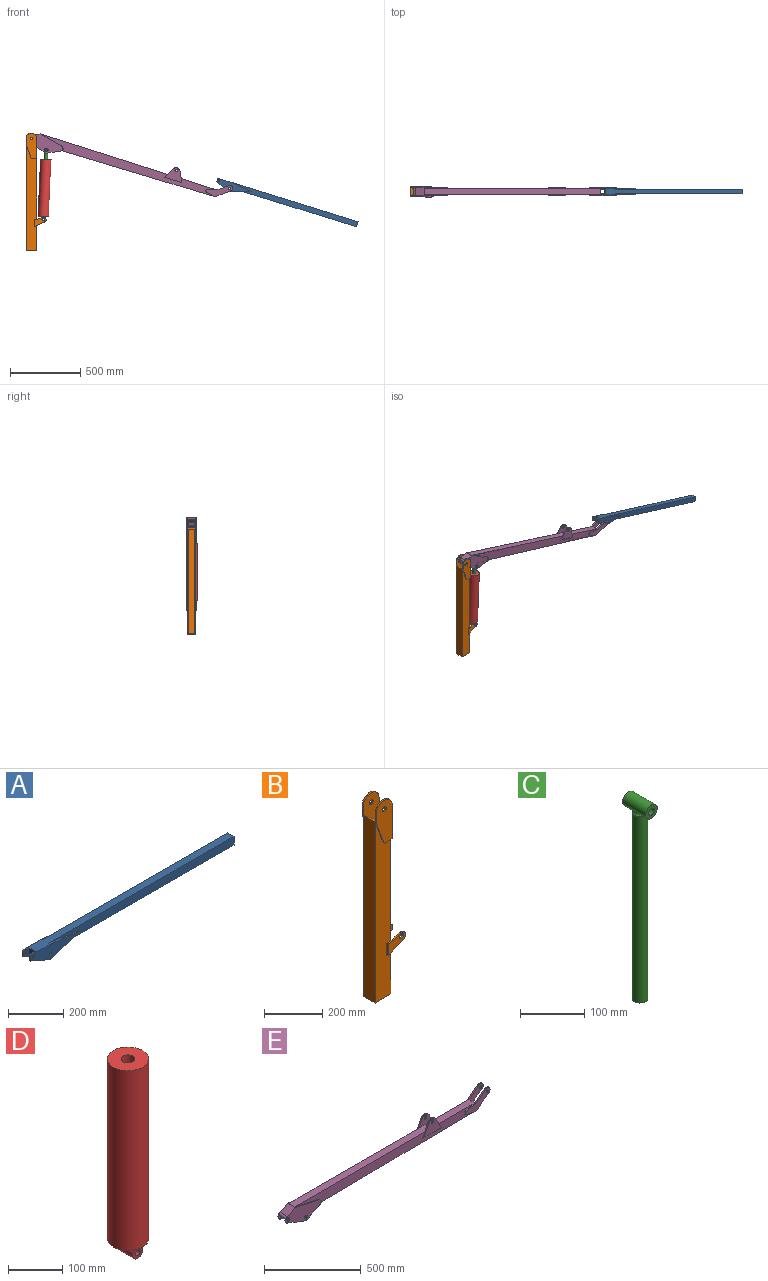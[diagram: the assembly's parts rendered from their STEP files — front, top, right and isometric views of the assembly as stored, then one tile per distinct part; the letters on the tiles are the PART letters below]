
ASSEMBLY  parts=5 mates=5
PART A: 24 faces, bbox 1045.2x44.5x69.9 mm
  f0: plane 945.69x38.1mm, normal (0,-1,0), area 32165.4mm2, adj f1,f3,f4,f7,f8
  f1: plane 1045.2x44.45mm, normal (0,0,1), area 33521.7mm2, adj f0,f2,f4,f5,f8,f10,f13,f14
  f2: plane 38.1x31.75mm, normal (-1,0,0), area 1209.7mm2, adj f1,f3,f5,f15
  f3: plane 1016x31.75mm, normal (0,0,-1), area 32258mm2, adj f0,f2,f4,f12,f14,f22
  f4: plane 38.1x31.75mm, normal (1,0,0), area 1209.7mm2, adj f0,f1,f3,f14
  f5: plane 38.1x29.2mm, normal (0,1,0), area 800.3mm2, adj f1,f2,f6,f9,f10
  f6: plane 102.19x44.45mm, normal (-0.4,0,-0.92), area 707.6mm2, adj f5,f7,f10,f12,f13
  f7: plane 151.53x50.8mm, normal (0.32,0,-0.95), area 1014.9mm2, adj f0,f6,f8,f12,f13
  f8: plane 154.22x19.05mm, normal (0.12,0,0.99), area 986.7mm2, adj f0,f1,f7,f13
  f9: cylinder r=6.35mm len=12.7mm, axis (0,-1,0), area 253.4mm2, adj f5,f13
  f10: plane 25.4x6.35mm, normal (-1,0,0), area 161.3mm2, adj f1,f5,f6,f13
  f11: cylinder r=6.35mm len=12.7mm, axis (0,-1,0), area 253.4mm2, adj f12,f13
  f12: plane 167.7x31.75mm, normal (0,1,0), area 2535.6mm2, adj f3,f6,f7,f11
  f13: plane 253.72x69.85mm, normal (0,-1,0), area 9880.1mm2, adj f1,f6,f7,f8,f9,f10,f11
  f14: plane 945.69x38.1mm, normal (0,1,0), area 32165.4mm2, adj f1,f3,f4,f17,f18
  f15: plane 38.1x29.2mm, normal (0,-1,0), area 800.3mm2, adj f1,f2,f16,f19,f20
  f16: plane 102.19x44.45mm, normal (-0.4,0,-0.92), area 707.6mm2, adj f15,f17,f20,f22,f23
  f17: plane 151.53x50.8mm, normal (0.32,0,-0.95), area 1014.9mm2, adj f14,f16,f18,f22,f23
  f18: plane 154.22x19.05mm, normal (0.12,0,0.99), area 986.7mm2, adj f1,f14,f17,f23
  f19: cylinder r=6.35mm len=12.7mm, axis (0,1,0), area 253.4mm2, adj f15,f23
  f20: plane 25.4x6.35mm, normal (-1,0,0), area 161.3mm2, adj f1,f15,f16,f23
  f21: cylinder r=6.35mm len=12.7mm, axis (0,1,0), area 253.4mm2, adj f22,f23
  f22: plane 167.7x31.75mm, normal (0,-1,0), area 2535.6mm2, adj f3,f16,f17,f21
  f23: plane 253.72x69.85mm, normal (0,1,0), area 9880.1mm2, adj f1,f16,f17,f18,f19,f20,f21
PART B: 56 faces, bbox 143.7x69.9x838.2 mm
  f0: plane 762x57.15mm, normal (-1,0,0), area 43548.3mm2, adj f1,f3,f4,f20
  f1: plane 76.2x57.15mm, normal (0,0,-1), area 4354.8mm2, adj f0,f2,f4,f20
  f2: plane 800.1x69.85mm, normal (1,0,0), area 41715.7mm2, adj f1,f3,f4,f7,f8,f10,f11,f12
  f3: plane 76.2x63.94mm, normal (0.64,0,0.77), area 5684.8mm2, adj f0,f2,f11,f27
  f4: plane 762x76.2mm, normal (0,-1,0), area 51151.3mm2, adj f0,f1,f2,f6,f7,f13,f14,f17
  f5: plane 38.1x6.35mm, normal (-1,0,0), area 241.9mm2, adj f6,f8,f10,f11
  f6: plane 105.33x38.1mm, normal (-0.94,0,-0.34), area 711.2mm2, adj f4,f5,f7,f10
  f7: plane 38.1x6.35mm, normal (0,0,-1), area 241.9mm2, adj f2,f4,f6,f10
  f8: cylinder r=38.1mm len=76.2mm, axis (0,1,0), area 760.1mm2, adj f2,f5,f10,f11
  f9: cylinder r=9.53mm len=19.05mm, axis (0,1,0), area 380mm2, adj f10,f11
  f10: plane 181.53x76.2mm, normal (0,-1,0), area 10917.7mm2, adj f2,f5,f6,f7,f8,f9
  f11: plane 140.14x76.2mm, normal (0,1,0), area 7334.5mm2, adj f2,f3,f5,f8,f9
  f12: plane 67.46x57.89mm, normal (0,1,0), area 2161.5mm2, adj f2,f14,f15,f16,f17,f18
  f13: plane 50.8x6.35mm, normal (-1,0,0), area 322.6mm2, adj f4,f14,f17,f19
  f14: plane 69.83x30.5mm, normal (0.4,0,-0.92), area 483.9mm2, adj f4,f12,f13,f15,f19
  f15: cylinder r=20.66mm len=17.38mm, axis (0,1,0), area 162.9mm2, adj f12,f14,f16,f19
  f16: cylinder r=20.58mm len=27.25mm, axis (0,1,0), area 234.7mm2, adj f12,f15,f17,f19
  f17: cylinder r=130.25mm len=59.19mm, axis (0,1,0), area 390.1mm2, adj f4,f12,f13,f16,f19
  f18: cylinder r=9.53mm len=19.05mm, axis (0,1,0), area 380mm2, adj f12,f19
  f19: plane 86.43x66.18mm, normal (0,-1,0), area 3055.3mm2, adj f13,f14,f15,f16,f17,f18
  f20: plane 762x76.2mm, normal (0,1,0), area 51151.3mm2, adj f0,f1,f2,f22,f23,f29,f30,f33
  f21: plane 38.1x6.35mm, normal (-1,0,0), area 241.9mm2, adj f22,f24,f26,f27
  f22: plane 105.33x38.1mm, normal (-0.94,0,-0.34), area 711.2mm2, adj f20,f21,f23,f26
  f23: plane 38.1x6.35mm, normal (0,0,-1), area 241.9mm2, adj f2,f20,f22,f26
  f24: cylinder r=38.1mm len=76.2mm, axis (0,-1,0), area 760.1mm2, adj f2,f21,f26,f27
  f25: cylinder r=9.53mm len=19.05mm, axis (0,-1,0), area 380mm2, adj f26,f27
  f26: plane 181.53x76.2mm, normal (0,1,0), area 10917.7mm2, adj f2,f21,f22,f23,f24,f25
  f27: plane 140.14x76.2mm, normal (0,-1,0), area 7334.5mm2, adj f2,f3,f21,f24,f25
  f28: plane 67.46x57.89mm, normal (0,-1,0), area 2161.5mm2, adj f2,f30,f31,f32,f33,f34
  f29: plane 50.8x6.35mm, normal (-1,0,0), area 322.6mm2, adj f20,f30,f33,f35
  f30: plane 69.83x30.5mm, normal (0.4,0,-0.92), area 483.9mm2, adj f20,f28,f29,f31,f35
  f31: cylinder r=20.66mm len=17.38mm, axis (0,-1,0), area 162.9mm2, adj f28,f30,f32,f35
  f32: cylinder r=20.58mm len=27.25mm, axis (0,-1,0), area 234.7mm2, adj f28,f31,f33,f35
  f33: cylinder r=130.25mm len=59.19mm, axis (0,-1,0), area 390.1mm2, adj f20,f28,f29,f32,f35
  f34: cylinder r=9.53mm len=19.05mm, axis (0,-1,0), area 380mm2, adj f28,f35
  f35: plane 86.43x66.18mm, normal (0,1,0), area 3055.3mm2, adj f29,f30,f31,f32,f33,f34
  f36: plane 34.9x6.35mm, normal (1,0,0), area 221.6mm2, adj f37,f39,f40,f43
  f37: plane 6.35x6.27mm, normal (-0.4,0,0.92), area 43.4mm2, adj f36,f40,f43,f45
  f38: plane 27.29x6.35mm, normal (0,0,1), area 173.3mm2, adj f41,f42,f43,f45
  f39: cylinder r=136.6mm len=6.35mm, axis (0,1,0), area 39.9mm2, adj f36,f40,f43,f45
  f40: plane 35.33x6.27mm, normal (0,1,0), area 211.4mm2, adj f36,f37,f39,f45
  f41: plane 78.94x28.55mm, normal (0.94,0,0.34), area 533mm2, adj f38,f42,f43,f44
  f42: plane 78.94x55.85mm, normal (0,1,0), area 1973mm2, adj f38,f41,f44,f45
  f43: plane 742.03x63.5mm, normal (0,1,0), area 43243mm2, adj f36,f37,f38,f39,f41,f44,f45,f46
  f44: plane 63.5x57.15mm, normal (-0.64,0,-0.77), area 4610.5mm2, adj f41,f42,f43,f45,f47,f53,f54,f55
  f45: plane 688.75x57.15mm, normal (-1,0,0), area 31436.2mm2, adj f37,f38,f39,f40,f42,f43,f44,f46
  f46: plane 63.5x44.45mm, normal (0,0,1), area 2822.6mm2, adj f43,f45,f47,f55
  f47: plane 742.03x44.45mm, normal (1,0,0), area 32983.3mm2, adj f43,f44,f46,f55
  f48: plane 34.9x6.35mm, normal (1,0,0), area 221.6mm2, adj f49,f51,f52,f55
  f49: cylinder r=136.6mm len=6.35mm, axis (0,-1,0), area 39.9mm2, adj f45,f48,f52,f55
  f50: plane 27.29x6.35mm, normal (0,0,1), area 173.3mm2, adj f45,f53,f54,f55
  f51: plane 6.35x6.27mm, normal (-0.4,0,0.92), area 43.4mm2, adj f45,f48,f52,f55
  f52: plane 35.33x6.27mm, normal (0,-1,0), area 211.4mm2, adj f45,f48,f49,f51
  f53: plane 78.94x55.85mm, normal (0,-1,0), area 1973mm2, adj f44,f45,f50,f54
  f54: plane 78.94x28.55mm, normal (0.94,0,0.34), area 533mm2, adj f44,f50,f53,f55
  f55: plane 742.03x63.5mm, normal (0,-1,0), area 43243mm2, adj f44,f45,f46,f47,f48,f49,f50,f51
PART C: 7 faces, bbox 30.4x50.8x382.3 mm
  f0: torus R=14.04mm, axis (0,0,-1), area 301.1mm2, adj f1,f4
  f1: cylinder r=12.45mm len=355.6mm, axis (0,0,-1), area 27808.1mm2, adj f0,f2
  f2: plane 24.89x24.89mm, normal (0,0,-1), area 486.6mm2, adj f1
  f3: cylinder r=6.35mm len=50.8mm, axis (0,1,0), area 2026.8mm2, adj f5,f6
  f4: cylinder r=12.7mm len=50.8mm, axis (0,1,0), area 3734.6mm2, adj f0,f5,f6
  f5: plane 25.4x25.4mm, normal (0,-1,0), area 380mm2, adj f3,f4
  f6: plane 25.4x25.4mm, normal (0,1,0), area 380mm2, adj f3,f4
PART D: 14 faces, bbox 76.2x76.2x438.3 mm
  f0: torus R=23.27mm, axis (0,0,-1), area 1438.7mm2, adj f1,f7
  f1: plane 76.2x76.2mm, normal (0,0,-1), area 3128mm2, adj f0,f5
  f2: plane 25.4x25.4mm, normal (0,0,1), area 506.7mm2, adj f3
  f3: cylinder r=12.7mm len=393.7mm, axis (0,0,-1), area 31415.9mm2, adj f2,f4
  f4: plane 76.2x76.2mm, normal (0,0,1), area 4053.7mm2, adj f3,f5
  f5: cylinder r=38.1mm len=406.4mm, axis (0,0,-1), area 97287.8mm2, adj f1,f4
  f6: cylinder r=6.35mm len=50.8mm, axis (0,1,0), area 2020.7mm2, adj f8,f9,f10,f11,f12,f13
  f7: cylinder r=12.7mm len=50.8mm, axis (0,1,0), area 3535.6mm2, adj f0,f8,f9
  f8: plane 25.4x25.4mm, normal (0,-1,0), area 380mm2, adj f6,f7
  f9: plane 25.4x25.4mm, normal (0,1,0), area 380mm2, adj f6,f7
  f10: sphere r=12.7mm, area 12.5mm2, adj f6,f11
  f11: torus R=23.27mm, axis (0,0,-1), area 11.6mm2, adj f6,f10
  f12: sphere r=12.7mm, area 12.5mm2, adj f6,f13
  f13: torus R=23.27mm, axis (0,0,-1), area 11.6mm2, adj f6,f12
PART E: 96 faces, bbox 1494.5x57.2x182.7 mm
  f0: plane 1320.8x66.61mm, normal (0,-1,0), area 64856.4mm2, adj f2,f4,f13,f18,f19,f20,f24,f25
  f1: plane 57.15x55.97mm, normal (-0.47,0,0.88), area 3629mm2, adj f2,f6,f13,f15,f42,f44
  f2: plane 1320.8x44.45mm, normal (0,0,1), area 58709.6mm2, adj f0,f1,f3,f16,f35,f45
  f3: plane 44.45x38.1mm, normal (1,0,0), area 1693.5mm2, adj f2,f23,f52,f64
  f4: plane 1326.63x44.45mm, normal (0.01,0,-1), area 58974.4mm2, adj f0,f5,f7,f35,f36,f64
  f5: cylinder r=38.1mm len=49.59mm, axis (0,-1,0), area 2894.1mm2, adj f4,f6,f7,f36
  f6: cylinder r=21.02mm len=57.15mm, axis (0,-1,0), area 1338.5mm2, adj f1,f5,f7,f11,f15,f36,f40,f44
  f7: plane 254.02x80.78mm, normal (0,1,0), area 7157.6mm2, adj f4,f5,f6,f8,f9,f10,f11,f12
  f8: plane 88.01x43.23mm, normal (0.44,0,-0.9), area 622.6mm2, adj f7,f15,f32,f33
  f9: plane 122.7x47.51mm, normal (-0.36,0,-0.93), area 835.5mm2, adj f7,f10,f15,f32
  f10: plane 6.82x6.35mm, normal (-0.01,0,1), area 43.3mm2, adj f7,f9,f11,f15
  f11: cylinder r=9.53mm len=11.11mm, axis (0,-1,0), area 76.5mm2, adj f6,f7,f10,f15
  f12: cylinder r=9.53mm len=19.05mm, axis (0,-1,0), area 380mm2, adj f7,f15
  f13: plane 169.2x35.96mm, normal (0.21,0,0.98), area 1098.4mm2, adj f0,f1,f15,f34
  f14: cylinder r=9.53mm len=19.05mm, axis (0,-1,0), area 380mm2, adj f7,f15
  f15: plane 259.23x119.17mm, normal (0,-1,0), area 18317.6mm2, adj f1,f6,f8,f9,f10,f11,f12,f13
  f16: plane 101.49x63.5mm, normal (0,1,0), area 4014.6mm2, adj f2,f17,f18,f20,f21
  f17: cylinder r=30.57mm len=54.63mm, axis (0,-1,0), area 429.1mm2, adj f16,f18,f20,f22
  f18: plane 72.05x36.18mm, normal (0.89,0,0.45), area 512mm2, adj f0,f16,f17,f19,f22
  f19: plane 127x6.35mm, normal (0,0,-1), area 806.5mm2, adj f0,f18,f20,f22
  f20: plane 72.05x36.18mm, normal (-0.89,0,0.45), area 512mm2, adj f0,f16,f17,f19,f22
  f21: cylinder r=9.53mm len=19.05mm, axis (0,-1,0), area 380mm2, adj f16,f22
  f22: plane 127x88.9mm, normal (0,-1,0), area 6916.4mm2, adj f17,f18,f19,f20,f21
  f23: plane 113.47x108.72mm, normal (0,1,0), area 4797.5mm2, adj f3,f26,f27,f28,f29,f30,f64
  f24: plane 17.14x6.35mm, normal (-1,0,0), area 108.9mm2, adj f0,f25,f29,f31
  f25: plane 74.32x16.83mm, normal (-0.22,0,0.98), area 483.9mm2, adj f0,f24,f26,f31
  f26: plane 70.77x53.8mm, normal (-0.61,0,0.8), area 564.5mm2, adj f23,f25,f27,f31
  f27: cylinder r=20.22mm len=36.32mm, axis (0,-1,0), area 403.4mm2, adj f23,f26,f28,f31
  f28: plane 95.25x72.4mm, normal (0.61,0,-0.8), area 759.7mm2, adj f23,f27,f29,f31
  f29: plane 74.32x16.83mm, normal (-0.22,0,-0.98), area 483.9mm2, adj f0,f23,f24,f28,f31
  f30: cylinder r=6.35mm len=12.7mm, axis (0,-1,0), area 253.4mm2, adj f23,f31
  f31: plane 177.55x108.72mm, normal (0,-1,0), area 7257.2mm2, adj f24,f25,f26,f27,f28,f29,f30
  f32: cylinder r=25.4mm len=20.37mm, axis (0,-1,0), area 133.2mm2, adj f7,f8,f9,f15
  f33: cylinder r=25.4mm len=17.66mm, axis (0,1,0), area 146.9mm2, adj f0,f7,f8,f15,f34
  f34: cylinder r=25.4mm len=19.71mm, axis (0,-1,0), area 186.7mm2, adj f0,f13,f15,f33
  f35: plane 1320.8x66.61mm, normal (0,1,0), area 64856.4mm2, adj f2,f4,f42,f47,f48,f49,f53,f54
  f36: plane 254.02x80.78mm, normal (0,-1,0), area 7157.6mm2, adj f4,f5,f6,f37,f38,f39,f40,f41
  f37: plane 88.01x43.23mm, normal (0.44,0,-0.9), area 622.6mm2, adj f36,f44,f61,f62
  f38: plane 122.7x47.51mm, normal (-0.36,0,-0.93), area 835.5mm2, adj f36,f39,f44,f61
  f39: plane 6.82x6.35mm, normal (-0.01,0,1), area 43.3mm2, adj f36,f38,f40,f44
  f40: cylinder r=9.53mm len=11.11mm, axis (0,1,0), area 76.5mm2, adj f6,f36,f39,f44
  f41: cylinder r=9.53mm len=19.05mm, axis (0,1,0), area 380mm2, adj f36,f44
  f42: plane 169.2x35.96mm, normal (0.21,0,0.98), area 1098.4mm2, adj f1,f35,f44,f63
  f43: cylinder r=9.53mm len=19.05mm, axis (0,1,0), area 380mm2, adj f36,f44
  f44: plane 259.23x119.17mm, normal (0,1,0), area 18317.6mm2, adj f1,f6,f37,f38,f39,f40,f41,f42
  f45: plane 101.49x63.5mm, normal (0,-1,0), area 4014.6mm2, adj f2,f46,f47,f49,f50
  f46: cylinder r=30.57mm len=54.63mm, axis (0,1,0), area 429.1mm2, adj f45,f47,f49,f51
  f47: plane 72.05x36.18mm, normal (0.89,0,0.45), area 512mm2, adj f35,f45,f46,f48,f51
  f48: plane 127x6.35mm, normal (0,0,-1), area 806.5mm2, adj f35,f47,f49,f51
  f49: plane 72.05x36.18mm, normal (-0.89,0,0.45), area 512mm2, adj f35,f45,f46,f48,f51
  f50: cylinder r=9.53mm len=19.05mm, axis (0,1,0), area 380mm2, adj f45,f51
  f51: plane 127x88.9mm, normal (0,1,0), area 6916.4mm2, adj f46,f47,f48,f49,f50
  f52: plane 113.47x108.72mm, normal (0,-1,0), area 4797.5mm2, adj f3,f55,f56,f57,f58,f59,f64
  f53: plane 17.14x6.35mm, normal (-1,0,0), area 108.9mm2, adj f35,f54,f58,f60
  f54: plane 74.32x16.83mm, normal (-0.22,0,0.98), area 483.9mm2, adj f35,f53,f55,f60
  f55: plane 70.77x53.8mm, normal (-0.61,0,0.8), area 564.5mm2, adj f52,f54,f56,f60
  f56: cylinder r=20.22mm len=36.32mm, axis (0,1,0), area 403.4mm2, adj f52,f55,f57,f60
  f57: plane 95.25x72.4mm, normal (0.61,0,-0.8), area 759.7mm2, adj f52,f56,f58,f60
  f58: plane 74.32x16.83mm, normal (-0.22,0,-0.98), area 483.9mm2, adj f35,f52,f53,f57,f60
  f59: cylinder r=6.35mm len=12.7mm, axis (0,1,0), area 253.4mm2, adj f52,f60
  f60: plane 177.55x108.72mm, normal (0,1,0), area 7257.2mm2, adj f53,f54,f55,f56,f57,f58,f59
  f61: cylinder r=25.4mm len=20.37mm, axis (0,1,0), area 133.2mm2, adj f36,f37,f38,f44
  f62: cylinder r=25.4mm len=17.66mm, axis (0,-1,0), area 146.9mm2, adj f35,f36,f37,f44,f63
  f63: cylinder r=25.4mm len=19.71mm, axis (0,1,0), area 186.7mm2, adj f35,f42,f44,f62
  f64: plane 44.45x12.88mm, normal (0.71,0,-0.7), area 803.9mm2, adj f0,f3,f4,f23,f35,f52
  f65: cylinder r=19.05mm len=14.38mm, axis (0,-1,0), area 131.7mm2, adj f68,f69,f70,f76
  f66: plane 7x6.35mm, normal (1,0,0), area 44.4mm2, adj f71,f72,f73,f76
  f67: plane 106.41x6.35mm, normal (0,0,1), area 675.7mm2, adj f74,f75,f76,f77
  f68: plane 166.92x35.48mm, normal (-0.21,0,-0.98), area 1083.6mm2, adj f65,f69,f76,f82
  f69: plane 230.03x56.31mm, normal (0,1,0), area 7805mm2, adj f65,f68,f70,f80,f81,f82
  f70: cylinder r=19.05mm len=6.35mm, axis (0,1,0), area 32.1mm2, adj f65,f69,f76,f80
  f71: plane 61.62x13.95mm, normal (0.22,0,0.98), area 401.2mm2, adj f66,f73,f76,f79
  f72: plane 61.62x13.95mm, normal (0.22,0,-0.98), area 401.2mm2, adj f66,f73,f76,f79
  f73: plane 61.62x34.9mm, normal (0,1,0), area 1290.9mm2, adj f66,f71,f72,f79
  f74: plane 106.41x12.7mm, normal (0,1,0), area 1270.4mm2, adj f67,f75,f77,f78
  f75: plane 12.7x6.38mm, normal (-0.89,0,-0.45), area 90.2mm2, adj f67,f74,f76,f78
  f76: plane 1313.5x53.96mm, normal (0,1,0), area 53183.4mm2, adj f65,f66,f67,f68,f70,f71,f72,f75
  f77: plane 12.7x6.38mm, normal (0.89,0,-0.45), area 90.2mm2, adj f67,f74,f76,f78
  f78: plane 1312.86x44.45mm, normal (0,0,-1), area 42872.6mm2, adj f74,f75,f76,f77,f79,f82,f92,f93
  f79: plane 44.45x38.19mm, normal (-1,0,0), area 1655.7mm2, adj f71,f72,f73,f76,f78,f80,f89,f90
  f80: plane 1328.06x44.45mm, normal (-0.01,0,1), area 44632.7mm2, adj f69,f70,f76,f79,f81,f87,f88,f92
  f81: cylinder r=44.45mm len=44.45mm, axis (0,-1,0), area 2127.5mm2, adj f69,f80,f82,f87
  f82: plane 49.36x44.45mm, normal (0.47,0,-0.88), area 2479.9mm2, adj f68,f69,f76,f78,f81,f86,f87,f92
  f83: cylinder r=19.05mm len=14.38mm, axis (0,1,0), area 131.7mm2, adj f86,f87,f88,f92
  f84: plane 7x6.35mm, normal (1,0,0), area 44.4mm2, adj f89,f90,f91,f92
  f85: plane 106.41x6.35mm, normal (0,0,1), area 675.7mm2, adj f92,f93,f94,f95
  f86: plane 166.92x35.48mm, normal (-0.21,0,-0.98), area 1083.6mm2, adj f82,f83,f87,f92
  f87: plane 230.03x56.31mm, normal (0,-1,0), area 7805mm2, adj f80,f81,f82,f83,f86,f88
  f88: cylinder r=19.05mm len=6.35mm, axis (0,-1,0), area 32.1mm2, adj f80,f83,f87,f92
  f89: plane 61.62x13.95mm, normal (0.22,0,-0.98), area 401.2mm2, adj f79,f84,f91,f92
  f90: plane 61.62x13.95mm, normal (0.22,0,0.98), area 401.2mm2, adj f79,f84,f91,f92
  f91: plane 61.62x34.9mm, normal (0,-1,0), area 1290.9mm2, adj f79,f84,f89,f90
  f92: plane 1313.5x53.96mm, normal (0,-1,0), area 53183.4mm2, adj f78,f79,f80,f82,f83,f84,f85,f86
  f93: plane 12.7x6.38mm, normal (-0.89,0,-0.45), area 90.2mm2, adj f78,f85,f92,f94
  f94: plane 106.41x12.7mm, normal (0,-1,0), area 1270.4mm2, adj f78,f85,f93,f95
  f95: plane 12.7x6.38mm, normal (0.89,0,-0.45), area 90.2mm2, adj f78,f85,f92,f94
PLACE A rot(axis=(0,1,0),17.2deg) t=(-995.18,-38.44,-74.76)mm
PLACE B t=(-844.86,-38.44,-43.56)mm fixed
PLACE C rot(axis=(0,1,0),2.5deg) t=(-815.87,-13.04,-62)mm
PLACE D rot(axis=(0,1,0),2.5deg) t=(-817.68,-13.04,-103.42)mm
PLACE E rot(axis=(0,1,0),17.6deg) t=(-995.95,-38.44,-64.61)mm
MATE revolute B.f8 <-> E.f6  axis (0,1,0) through (-905.97,-38.44,399.8)mm
MATE slider C.f0 <-> D.f0  axis (-0.04,0,-1) through (-815.41,-13.04,-51.58)mm
MATE revolute A.f11 <-> E.f27  axis (0,-1,0) through (505.81,-32.09,44.23)mm
MATE revolute D.f7 <-> B.f15  axis (0,-1,0) through (-820.86,-38.44,-176.29)mm
MATE cylindrical E.f12 <-> C.f4  axis (0,1,0) through (-799.28,-32.09,317.62)mm
